# Revit family: REBS
name_source: partatom
category: Mechanical Equipment
units: mm (PartAtom-declared; Revit-internal decimal feet)

## family parameters
Always vertical = Yes
Cut with Voids When Loaded = No
Part Type = Normal
Room Calculation Point = No
Round Connector Dimension = Use Diameter
Shared = No
Work Plane-Based = No

## types (4) — shared parameters
0 = 0' - 0"
1" = 0' - 1"
1.5 = 0' - 1 1/2"
2" = 0' - 2"
2' = 2' - 0"
4" = 0' - 4"
Manufacturer = Loren Cook Company
Model = REBS
ONE EIGTH = 0' - 0 1/8"
Type Comments = Downblast Propeller Supply Ventilator Roof Mounted/Direct Drive
URL = www.lorencook.com

## per-type parameters (varying)
| type | (T_SQ/2)-2" | -(A/2) | -(C/2) | A | A-1.5" | A-B | A/2 | B | B-C | B-C/2 | B/2 | C | C-.125 | D | D/2 | D/2-(A-B) | RO | RO/2 | T_SQ | T_SQ/2 | T_SQ/2+.125" |
| 12_REBS | 0' - 8" | -0' - 7 9/32" | -0' - 1" | 1' - 2 9/16" | 1' - 1 1/16" | 0' - 9 7/16" | 0' - 7 9/32" | 0' - 5 1/8" | 0' - 3 1/8" | 0' - 1 9/16" | 0' - 2 9/16" | 0' - 2" | 0' - 1 7/8" | 2' - 4 1/4" | 1' - 2 1/8" | 0' - 4 11/16" | 1' - 3 1/2" | 0' - 7 3/4" | 1' - 8" | 0' - 10" | 0' - 10 1/8" |
| 16_REBS | 1' - 0" | -0' - 8" | -0' - 1" | 1' - 4" | 1' - 2 1/2" | 0' - 9 7/8" | 0' - 8" | 0' - 6 1/8" | 0' - 4 1/8" | 0' - 2 1/16" | 0' - 3 1/16" | 0' - 2" | 0' - 1 7/8" | 2' - 9 1/4" | 1' - 4 5/8" | 0' - 6 3/4" | 1' - 11 1/2" | 0' - 11 3/4" | 2' - 4" | 1' - 2" | 1' - 2 1/8" |
| 20_REBS | 1' - 2" | -0' - 9 3/16" | -0' - 1" | 1' - 6 3/8" | 1' - 4 7/8" | 0' - 11 1/4" | 0' - 9 3/16" | 0' - 7 1/8" | 0' - 5 1/8" | 0' - 2 9/16" | 0' - 3 9/16" | 0' - 2" | 0' - 1 7/8" | 3' - 7 1/4" | 1' - 9 5/8" | 0' - 10 3/8" | 2' - 3 1/2" | 1' - 1 3/4" | 2' - 8" | 1' - 4" | 1' - 4 1/8" |
| 24_REBS | 1' - 4" | -0' - 10 13/16" | -0' - 1 1/2" | 1' - 9 5/8" | 1' - 8 1/8" | 1' - 0 1/2" | 0' - 10 13/16" | 0' - 9 1/8" | 0' - 6 1/8" | 0' - 3 1/16" | 0' - 4 9/16" | 0' - 3" | 0' - 2 7/8" | 3' - 11 1/2" | 1' - 11 3/4" | 0' - 11 1/4" | 2' - 7 1/2" | 1' - 3 3/4" | 3' - 0" | 1' - 6" | 1' - 6 1/8" |

## geometry (parser evidence)
native form markers: Sweep x2
no freeform markers — native parametric forms only
